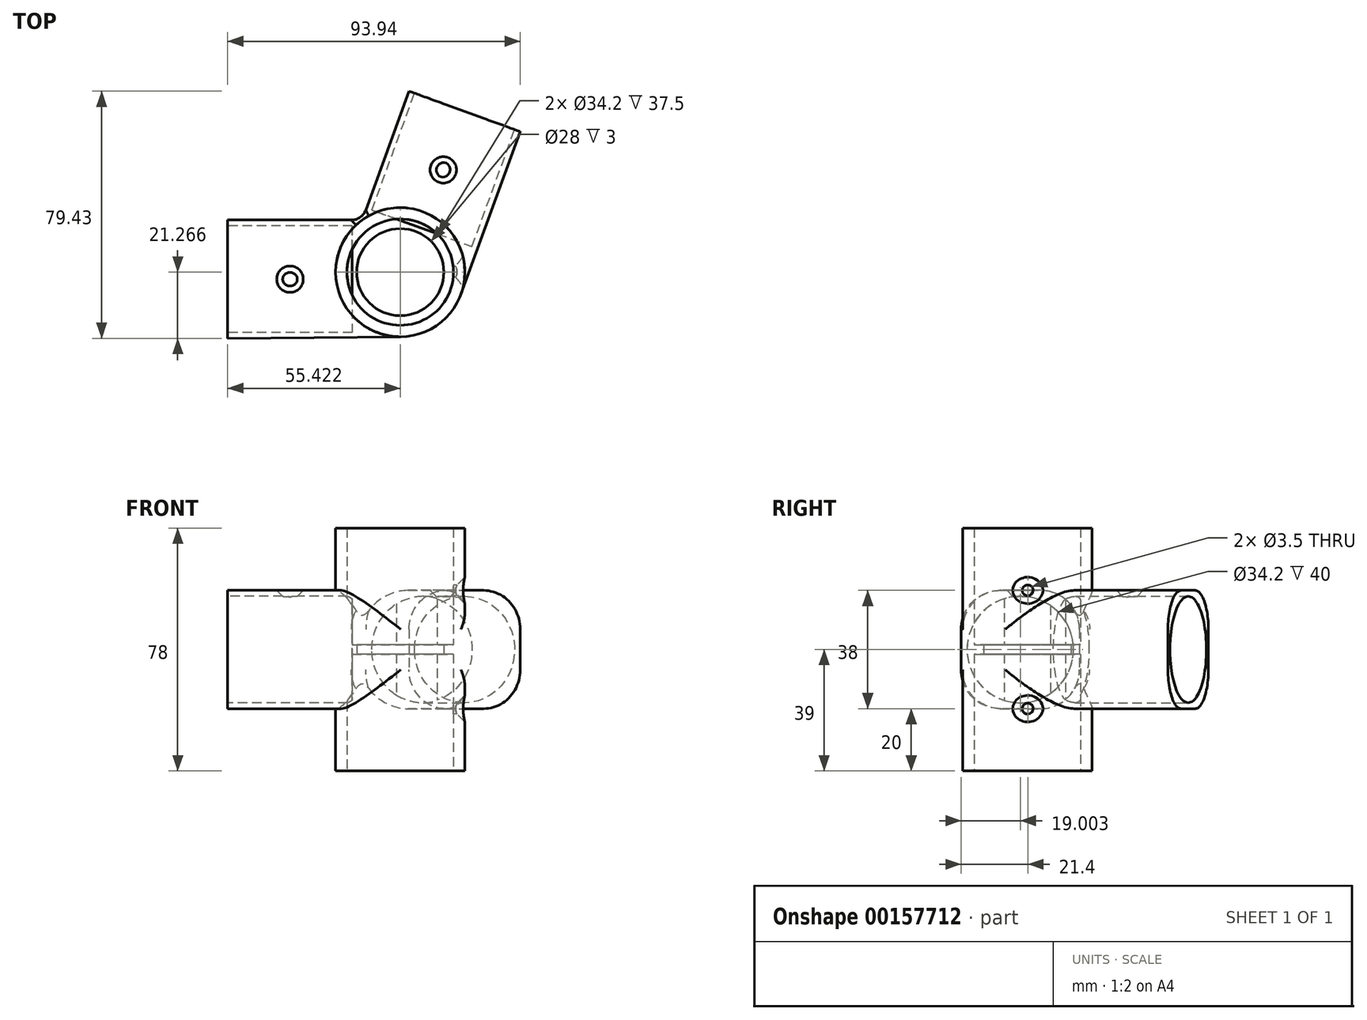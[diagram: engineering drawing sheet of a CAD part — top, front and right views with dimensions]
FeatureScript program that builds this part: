
annotation { "Feature Type Name" : "Feature", "Feature Type Description" : "" }
export const myFeature = defineFeature(function(context is Context, id is Id, definition is map)
    precondition{}
    {
        {
            var Q0;
            Q0=qCreatedBy(makeId("Top.planeOp"),FACE);
            var sketch = newSketch(context, id + "F0", { "sketchPlane" : qUnion([Q0])});
            skLineSegment(sketch, "E0.bottom", {"start": v(0, 0) * mm, "end": v(-70, -0.65) * mm});
            skLineSegment(sketch, "E0.right", {"start": v(-70, -0.65) * mm, "end": v(-70, 37.35) * mm});
            skLineSegment(sketch, "E1", {"start": v(0, 0) * mm, "end": v(23.94, 65.78) * mm});
            skLineSegment(sketch, "E2", {"start": v(-26.84, 37.35) * mm, "end": v(-11.77, 78.78) * mm});
            skLineSegment(sketch, "E3", {"start": v(-11.77, 78.78) * mm, "end": v(23.94, 65.78) * mm});
            skCircle(sketch, "E4", {"center": v(-14.58, 20.62) * mm, "radius": 20.75 * mm});
            skLineSegment(sketch, "E5", {"start": v(-14.82, 20.75) * mm, "end": v(0, 0) * mm, "construction": true});
            skCircle(sketch, "E6", {"center": v(-14.58, 20.62) * mm, "radius": 17.1 * mm});
            skLineSegment(sketch, "E7.trimOffspring", {"start": v(-26.84, 37.35) * mm, "end": v(-70, 37.35) * mm});
            skPoint(sketch, "E8", {"position": v(6.09, 72.28) * mm});
            skPoint(sketch, "E9", {"position": v(-70, 18.35) * mm});
            skLineSegment(sketch, "E10", {"start": v(6.09, 72.28) * mm, "end": v(-0.75, 53.48) * mm, "construction": true});
            skLineSegment(sketch, "E11", {"start": v(-70, 18.35) * mm, "end": v(-50, 18.35) * mm, "construction": true});
            skCircle(sketch, "E12", {"center": v(-50, 18.35) * mm, "radius": 1.75 * mm});
            skCircle(sketch, "E13", {"center": v(-0.75, 53.48) * mm, "radius": 1.75 * mm});
            skCircle(sketch, "E14", {"center": v(-14.58, 20.62) * mm, "radius": 14 * mm});
            skSolve(sketch);
        }
        {
            var Q0;
            {var subQ4=sQuery(id+"F0.wireOp",EDGE,"E0.right");Q0=makeQuery(id+"F0.imprint","IMPRINT",FACE,{"disambiguationData":[TD([[makeQuery(id+"F0.imprint","IMPRINT",EDGE,{"derivedFrom":subQ4}),-1.0]])]});}
            var Q1;
            Q1=makeQuery(id+"F0.imprint","IMPRINT",FACE,{"disambiguationData":[TD([[makeQuery(id+"F0.imprint","IMPRINT",EDGE,{"derivedFrom":sQuery(id+"F0.wireOp",EDGE,"E12")}),1.0]])]});
            var Q2;
            {var subQ1=sQuery(id+"F0.wireOp",EDGE,"E2");Q2=makeQuery(id+"F0.imprint","IMPRINT",FACE,{"disambiguationData":[TD([[makeQuery(id+"F0.imprint","IMPRINT",EDGE,{"derivedFrom":subQ1}),-1.0]])]});}
            var Q3;
            Q3=makeQuery(id+"F0.imprint","IMPRINT",FACE,{"disambiguationData":[TD([[makeQuery(id+"F0.imprint","IMPRINT",EDGE,{"derivedFrom":sQuery(id+"F0.wireOp",EDGE,"E13")}),1.0]])]});
            extrude(context, id + "F1", {"entities" : qUnion([Q0, Q1, Q2, Q3]), "depth" : 38 * mm});
        }
        {
            var Q0;
            Q0=makeQuery(id+"F0.imprint","IMPRINT",FACE,{"disambiguationData":[TD([[makeQuery(id+"F0.imprint","IMPRINT",EDGE,{"derivedFrom":sQuery(id+"F0.wireOp",EDGE,"E6")}),-1.0]])]});
            extrude(context, id + "F2", {"entities" : qUnion([Q0]), "operationType" : NewBodyOperationType.ADD, "depth" : 58 * mm, "hasSecondDirection" : true, "secondDirectionOppositeDirection" : true, "secondDirectionDepth" : 20 * mm});
        }
        {
            var Q0;
            Q0=makeQuery(id+"F0.imprint","IMPRINT",FACE,{"disambiguationData":[TD([[makeQuery(id+"F0.imprint","IMPRINT",EDGE,{"derivedFrom":sQuery(id+"F0.wireOp",EDGE,"E6")}),1.0]])]});
            extrude(context, id + "F3", {"entities" : qUnion([Q0]), "operationType" : NewBodyOperationType.ADD, "depth" : 20.5 * mm, "hasSecondDirection" : true, "secondDirectionOppositeDirection" : false, "secondDirectionDepth" : 17.5 * mm});
        }
        {
            var Q0;
            {var subQ0=sQuery(id+"F0.wireOp",EDGE,"E0.bottom");Q0=makeQuery(id+"F2.boolean.opBoolean","MERGE",EDGE,{"derivedFrom":[makeQuery(id+"F1.opExtrude","CAP_EDGE",EDGE,{"disambiguationData":[OSD([subQ0])],"isStart":true}),makeQuery(id+"F2.opExtrude","CAP_EDGE",EDGE,{"disambiguationData":[OSD([subQ0])],"isStart":true})]});}
            var Q1;
            Q1=makeQuery(id+"F1.opExtrude","CAP_EDGE",EDGE,{"disambiguationData":[OSD([sQuery(id+"F0.wireOp",EDGE,"E0.bottom")])],"isStart":false});
            var Q2;
            Q2=makeQuery(id+"F1.opExtrude","CAP_EDGE",EDGE,{"disambiguationData":[OSD([sQuery(id+"F0.wireOp",EDGE,"E1")])],"isStart":false});
            var Q3;
            {var subQ0=sQuery(id+"F0.wireOp",EDGE,"E1");Q3=makeQuery(id+"F2.boolean.opBoolean","MERGE",EDGE,{"derivedFrom":[makeQuery(id+"F1.opExtrude","CAP_EDGE",EDGE,{"disambiguationData":[OSD([subQ0])],"isStart":true}),makeQuery(id+"F2.opExtrude","CAP_EDGE",EDGE,{"disambiguationData":[OSD([subQ0])],"isStart":true})]});}
            fillet(context, id + "F4", {"entities" : qUnion([Q0, Q1, Q2, Q3]), "radius" : 12.5 * mm, "allowEdgeOverflow" : false});
        }
        {
            var Q0;
            Q0=makeQuery(id+"F1.opExtrude","CAP_EDGE",EDGE,{"disambiguationData":[OSD([sQuery(id+"F0.wireOp",EDGE,"E2")])],"isStart":false});
            fillet(context, id + "F5", {"entities" : qUnion([Q0]), "radius" : 12.5 * mm, "tangentPropagation" : true, "allowEdgeOverflow" : false});
        }
        {
            var Q0;
            Q0=makeQuery(id+"F1.opExtrude","CAP_EDGE",EDGE,{"disambiguationData":[OSD([sQuery(id+"F0.wireOp",EDGE,"E7.trimOffspring")])],"isStart":false});
            fillet(context, id + "F6", {"entities" : qUnion([Q0]), "radius" : 12.5 * mm, "tangentPropagation" : true, "allowEdgeOverflow" : false});
        }
        {
            var Q0;
            Q0=makeQuery(id+"F1.opExtrude","CAP_EDGE",EDGE,{"disambiguationData":[OSD([sQuery(id+"F0.wireOp",EDGE,"E2")])],"isStart":true});
            fillet(context, id + "F7", {"entities" : qUnion([Q0]), "radius" : 12.5 * mm, "allowEdgeOverflow" : false});
        }
        {
            var Q0;
            Q0=makeQuery(id+"F1.opExtrude","CAP_EDGE",EDGE,{"disambiguationData":[OSD([sQuery(id+"F0.wireOp",EDGE,"E7.trimOffspring")])],"isStart":true});
            var Q1;
            Q1=makeQuery(id+"F1.opExtrude","CAP_EDGE",EDGE,{"disambiguationData":[OSD([sQuery(id+"F0.wireOp",EDGE,"E0.bottom")])],"isStart":true});
            var Q2;
            Q2=makeQuery(id+"F1.opExtrude","CAP_EDGE",EDGE,{"disambiguationData":[OSD([sQuery(id+"F0.wireOp",EDGE,"E1")])],"isStart":true});
            fillet(context, id + "F8", {"entities" : qUnion([Q0, Q1, Q2]), "radius" : 12.5 * mm, "allowEdgeOverflow" : false});
        }
        {
            var Q0;
            Q0=makeQuery(id+"F1.opExtrude","SWEPT_FACE",FACE,{"disambiguationData":[OSD([sQuery(id+"F0.wireOp",EDGE,"E0.right")])]});
            var sketch = newSketch(context, id + "F9", { "sketchPlane" : qUnion([Q0])});
            skCircle(sketch, "E15", {"center": v(-18.35, 19) * mm, "radius": 17.1 * mm});
            skLineSegment(sketch, "E16", {"start": v(-37.35, 19) * mm, "end": v(0.65, 19) * mm, "construction": true});
            skSolve(sketch);
        }
        {
            var Q0;
            Q0=makeQuery(id+"F9.imprint","IMPRINT",FACE,{"disambiguationData":[TD([[makeQuery(id+"F9.imprint","IMPRINT",EDGE,{"derivedFrom":sQuery(id+"F9.wireOp",EDGE,"E15")}),1.0]])]});
            extrude(context, id + "F10", {"entities" : qUnion([Q0]), "operationType" : NewBodyOperationType.REMOVE, "oppositeDirection" : true, "depth" : 40 * mm});
        }
        {
            var Q0;
            Q0=makeQuery(id+"F1.opExtrude","SWEPT_FACE",FACE,{"disambiguationData":[OSD([sQuery(id+"F0.wireOp",EDGE,"E3")])]});
            var sketch = newSketch(context, id + "F11", { "sketchPlane" : qUnion([Q0])});
            skCircle(sketch, "E17", {"center": v(19, 19) * mm, "radius": 17.1 * mm});
            skLineSegment(sketch, "E18", {"start": v(19, 38) * mm, "end": v(19, 0) * mm, "construction": true});
            skSolve(sketch);
        }
        {
            var Q0;
            Q0=makeQuery(id+"F11.imprint","IMPRINT",FACE,{"disambiguationData":[TD([[makeQuery(id+"F11.imprint","IMPRINT",EDGE,{"derivedFrom":sQuery(id+"F11.wireOp",EDGE,"E17")}),1.0]])]});
            extrude(context, id + "F12", {"entities" : qUnion([Q0]), "operationType" : NewBodyOperationType.REMOVE, "oppositeDirection" : true, "depth" : 40 * mm});
        }
        {
            var Q0;
            Q0=qCreatedBy(makeId("Right.planeOp"),FACE);
            var sketch = newSketch(context, id + "F13", { "sketchPlane" : qUnion([Q0])});
            skCircle(sketch, "E19", {"center": v(20.75, 38) * mm, "radius": 1.75 * mm});
            skLineSegment(sketch, "E20", {"start": v(16.54, 38) * mm, "end": v(24.96, 38) * mm, "construction": true});
            skCircle(sketch, "E21", {"center": v(20.75, 0) * mm, "radius": 1.75 * mm});
            skSolve(sketch);
        }
        {
            var Q0;
            Q0=makeQuery(id+"F0.imprint","IMPRINT",FACE,{"disambiguationData":[TD([[makeQuery(id+"F0.imprint","IMPRINT",EDGE,{"derivedFrom":sQuery(id+"F0.wireOp",EDGE,"E12")}),1.0]])]});
            var Q1;
            Q1=makeQuery(id+"F0.imprint","IMPRINT",FACE,{"disambiguationData":[TD([[makeQuery(id+"F0.imprint","IMPRINT",EDGE,{"derivedFrom":sQuery(id+"F0.wireOp",EDGE,"E13")}),1.0]])]});
            extrude(context, id + "F14", {"entities" : qUnion([Q0, Q1]), "operationType" : NewBodyOperationType.REMOVE, "depth" : 45 * mm, "hasSecondDirection" : true, "secondDirectionOppositeDirection" : false, "secondDirectionDepth" : 35 * mm});
        }
        {
            var Q0;
            Q0=makeQuery(id+"F13.imprint","IMPRINT",FACE,{"disambiguationData":[TD([[makeQuery(id+"F13.imprint","IMPRINT",EDGE,{"derivedFrom":sQuery(id+"F13.wireOp",EDGE,"E19")}),1.0]])]});
            var Q1;
            Q1=makeQuery(id+"F13.imprint","IMPRINT",FACE,{"disambiguationData":[TD([[makeQuery(id+"F13.imprint","IMPRINT",EDGE,{"derivedFrom":sQuery(id+"F13.wireOp",EDGE,"E21")}),1.0]])]});
            extrude(context, id + "F15", {"entities" : qUnion([Q0, Q1]), "operationType" : NewBodyOperationType.REMOVE, "depth" : 10 * mm});
        }
        {
            var Q0;
            Q0=makeQuery(id+"F14.boolean.opBoolean","INTERSECT",EDGE,{"derivedFrom":[makeQuery(id+"F5.opFillet","SPLIT",FACE,{"disambiguationData":[OD(1.0)],"derivedFrom":makeQuery(id+"F1.opExtrude","CAP_FACE",FACE,{"disambiguationData":[OSD([sQuery(id+"F0.wireOp",EDGE,"E0.bottom"),sQuery(id+"F0.wireOp",EDGE,"E0.right"),sQuery(id+"F0.wireOp",EDGE,"E1"),sQuery(id+"F0.wireOp",EDGE,"E2"),sQuery(id+"F0.wireOp",EDGE,"E3"),sQuery(id+"F0.wireOp",EDGE,"E4"),sQuery(id+"F0.wireOp",EDGE,"E7.trimOffspring")])],"isStart":false})}),makeQuery(id+"F14.opExtrude","SWEPT_FACE",FACE,{"disambiguationData":[OSD([sQuery(id+"F0.wireOp",EDGE,"E13")])]})]});
            var Q1;
            Q1=makeQuery(id+"F14.boolean.opBoolean","INTERSECT",EDGE,{"derivedFrom":[makeQuery(id+"F5.opFillet","SPLIT",FACE,{"disambiguationData":[OD(0.0)],"derivedFrom":makeQuery(id+"F1.opExtrude","CAP_FACE",FACE,{"disambiguationData":[OSD([sQuery(id+"F0.wireOp",EDGE,"E0.bottom"),sQuery(id+"F0.wireOp",EDGE,"E0.right"),sQuery(id+"F0.wireOp",EDGE,"E1"),sQuery(id+"F0.wireOp",EDGE,"E2"),sQuery(id+"F0.wireOp",EDGE,"E3"),sQuery(id+"F0.wireOp",EDGE,"E4"),sQuery(id+"F0.wireOp",EDGE,"E7.trimOffspring")])],"isStart":false})}),makeQuery(id+"F14.opExtrude","SWEPT_FACE",FACE,{"disambiguationData":[OSD([sQuery(id+"F0.wireOp",EDGE,"E12")])]})]});
            var Q2;
            {var subQ0=sQuery(id+"F0.wireOp",EDGE,"E4");Q2=makeQuery(id+"F15.boolean.opBoolean","INTERSECT",EDGE,{"derivedFrom":[makeQuery(id+"F2.opExtrude","SWEPT_FACE",FACE,{"disambiguationData":[OSD([subQ0]),TDD([makeQuery(id+"F0.imprint","IMPRINT",EDGE,{"disambiguationData":[TD([[makeQuery(id+"F0.imprint","INTERSECT",VERTEX,{"disambiguationData":[OD(0.0)],"derivedFrom":[sQuery(id+"F0.wireOp",EDGE,"E0.bottom"),subQ0]}),-1.0]])],"derivedFrom":subQ0})])]}),makeQuery(id+"F15.opExtrude","SWEPT_FACE",FACE,{"disambiguationData":[OSD([sQuery(id+"F13.wireOp",EDGE,"E19")])]})]});}
            var Q3;
            Q3=makeQuery(id+"F15.boolean.opBoolean","COPY",EDGE,{"disambiguationData":[OD(0.0)],"derivedFrom":makeQuery(id+"F15.opExtrude","CAP_EDGE",EDGE,{"disambiguationData":[OSD([sQuery(id+"F13.wireOp",EDGE,"E19")])],"isStart":true})});
            var Q4;
            {var subQ0=sQuery(id+"F0.wireOp",EDGE,"E4");Q4=makeQuery(id+"F15.boolean.opBoolean","INTERSECT",EDGE,{"derivedFrom":[makeQuery(id+"F2.opExtrude","SWEPT_FACE",FACE,{"disambiguationData":[OSD([subQ0]),TDD([makeQuery(id+"F0.imprint","IMPRINT",EDGE,{"disambiguationData":[TD([[makeQuery(id+"F0.imprint","INTERSECT",VERTEX,{"disambiguationData":[OD(1.0)],"derivedFrom":[sQuery(id+"F0.wireOp",EDGE,"E0.bottom"),subQ0]}),1.0]])],"derivedFrom":subQ0})])]}),makeQuery(id+"F15.opExtrude","SWEPT_FACE",FACE,{"disambiguationData":[OSD([sQuery(id+"F13.wireOp",EDGE,"E19")])]})]});}
            var Q5;
            Q5=makeQuery(id+"F15.boolean.opBoolean","COPY",EDGE,{"disambiguationData":[OD(1.0)],"derivedFrom":makeQuery(id+"F15.opExtrude","CAP_EDGE",EDGE,{"disambiguationData":[OSD([sQuery(id+"F13.wireOp",EDGE,"E19")])],"isStart":true})});
            var Q6;
            Q6=makeQuery(id+"F15.boolean.opBoolean","INTERSECT",EDGE,{"derivedFrom":[makeQuery(id+"F2.opExtrude","SWEPT_FACE",FACE,{"disambiguationData":[OSD([sQuery(id+"F0.wireOp",EDGE,"E4")])]}),makeQuery(id+"F15.opExtrude","SWEPT_FACE",FACE,{"disambiguationData":[OSD([sQuery(id+"F13.wireOp",EDGE,"E21")])]})]});
            chamfer(context, id + "F16", {"entities" : qUnion([Q0, Q1, Q2, Q3, Q4, Q5, Q6]), "width" : 2.5 * mm, "tangentPropagation" : true});
        }
        {
            var Q0;
            {var subQ0=sQuery(id+"F0.wireOp",EDGE,"E0.bottom");var subQ1=sQuery(id+"F0.wireOp",EDGE,"E4");var subQ2=sQuery(id+"F0.wireOp",EDGE,"E7.trimOffspring");var subQ3=sQuery(id+"F0.wireOp",EDGE,"E2");var subQ4=sQuery(id+"F0.wireOp",EDGE,"E1");Q0=makeQuery(id+"F2.boolean.opBoolean","MERGE",EDGE,{"derivedFrom":[makeQuery(id+"F1.opExtrude","SWEPT_EDGE",EDGE,{"disambiguationData":[OSD([subQ3,subQ1,subQ2]),ownerDisambiguation([makeQuery(id+"F0.imprint","IMPRINT",EDGE,{"disambiguationData":[TD([[makeQuery(id+"F0.imprint","INTERSECT",VERTEX,{"derivedFrom":[subQ4,sQuery(id+"F0.wireOp",EDGE,"E3")]}),1.0]])],"derivedFrom":subQ4})])]}),makeQuery(id+"F1.opExtrude","SWEPT_EDGE",EDGE,{"disambiguationData":[OSD([subQ3,subQ1,subQ2]),ownerDisambiguation([makeQuery(id+"F0.imprint","IMPRINT",EDGE,{"disambiguationData":[TD([[makeQuery(id+"F0.imprint","INTERSECT",VERTEX,{"derivedFrom":[subQ0,sQuery(id+"F0.wireOp",EDGE,"E0.right")]}),1.0]])],"derivedFrom":subQ0})])]})]});}
            fillet(context, id + "F17", {"entities" : qUnion([Q0]), "radius" : 5 * mm, "tangentPropagation" : true, "allowEdgeOverflow" : false});
        }
    });
